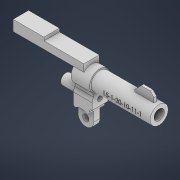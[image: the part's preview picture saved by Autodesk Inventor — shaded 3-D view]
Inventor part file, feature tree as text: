
AUTODESK INVENTOR PART (.ipt)
format: ipt  version: 2021 (Build 250183000, 183)  size: 522,752 bytes
history: native  units: in
note: dims shown in document units (in); Inventor stores cm internally (conversion verified against a paired STEP export)
features: extrude x11, sketch x11, plane x2, mirror x1, direct_edit x1, other x1
ambient origin geometry x8: Origin, YZ Plane, XZ Plane, XY Plane, X Axis, Y Axis, Z Axis, Center Point
bodies: Solid1 (feature_tree)
feature tree (27):
  extrude  "Extrusion1"  Depth=6.0in
  extrude  "Extrusion3"  Depth=12.0in
  extrude  "Extrusion4"  TaperAngle=0.0deg  [1 undecoded]
  plane  "Work Plane1"
  mirror  "Mirror1"
  extrude  "Extrusion5"  Depth=4.5in
  extrude  "Extrusion6"  Depth=12.0in
  extrude  "Extrusion7"  TaperAngle=0.0deg  [1 undecoded]
  extrude  "Extrusion8"  Depth=6.0in
  plane  "Work Plane2"
  extrude  "Extrusion10"  Depth=6.0in
  extrude  "Extrusion11"  Depth=8.517in
  extrude  "Extrusion12"  Depth=8.8891in
  direct_edit  "Direct Edit1"
  extrude  "Extrusion13"  TaperAngle=0.0deg  [1 undecoded]
  sketch  "Sketch1"  dims[d1=22.0in d2=6.0in]
  sketch  "Sketch2"  dims[d3=11.0in d4=12.0in]
  sketch  "Sketch3"  dims[d7=4.0in d8=0.0in]
  sketch  "Sketch5"  dims[d9=16.0in d10=4.5in]
  sketch  "Sketch6"  dims[d11=0.614in d12=12.0in]
  sketch  "Sketch7"  dims[d13=12.0in d14=0.0in]
  sketch  "Sketch8"  dims[d15=14.5in d16=0.0in d17=6.0in]
  sketch  "Sketch11"  dims[d19=16.0in d23=6.0in]
  sketch  "Sketch12"  dims[d24=1.0in d25=8.517in]
  sketch  "Sketch13"  dims[d26=2.0in d27=8.8891in]
  sketch  "Sketch15"  dims[d31=7.5in d32=0.0in d33=3.5in d34=0.0in d35=12.0in d36=5.0in d37=3.5in d38=0.0in d40=14.0in d41=46.0in d42=0.0in d43=8.0in d44=46.0in d45=0.0in d46=8.0in d47=12.0in d48=12.0in d49=0.0in d50=4.0in d51=12.0in d52=0.0in d64=-8.0in d65=55.0in d66=0.0in d67=2.5in d68=0.0in d69=31.0in d70=0.0in d71=3.0in d72=7.0in d73=15.0in d74=1.572in d75=0.0in d76=3.0in d77=5.0in d78=3.0in d79=1.0207in d80=2.0in d81=0.0in d82=0.0155in d83=0.3937in d84=0.3937in d91=0.3937in d92=0.0in d39=0.25in]
  other  "Scale1"
note: 3 required parameter values undecoded (feature->parameter linkage not recoverable at this tier; creation-order binding heuristic only, values carry confidence <= 0.55)
